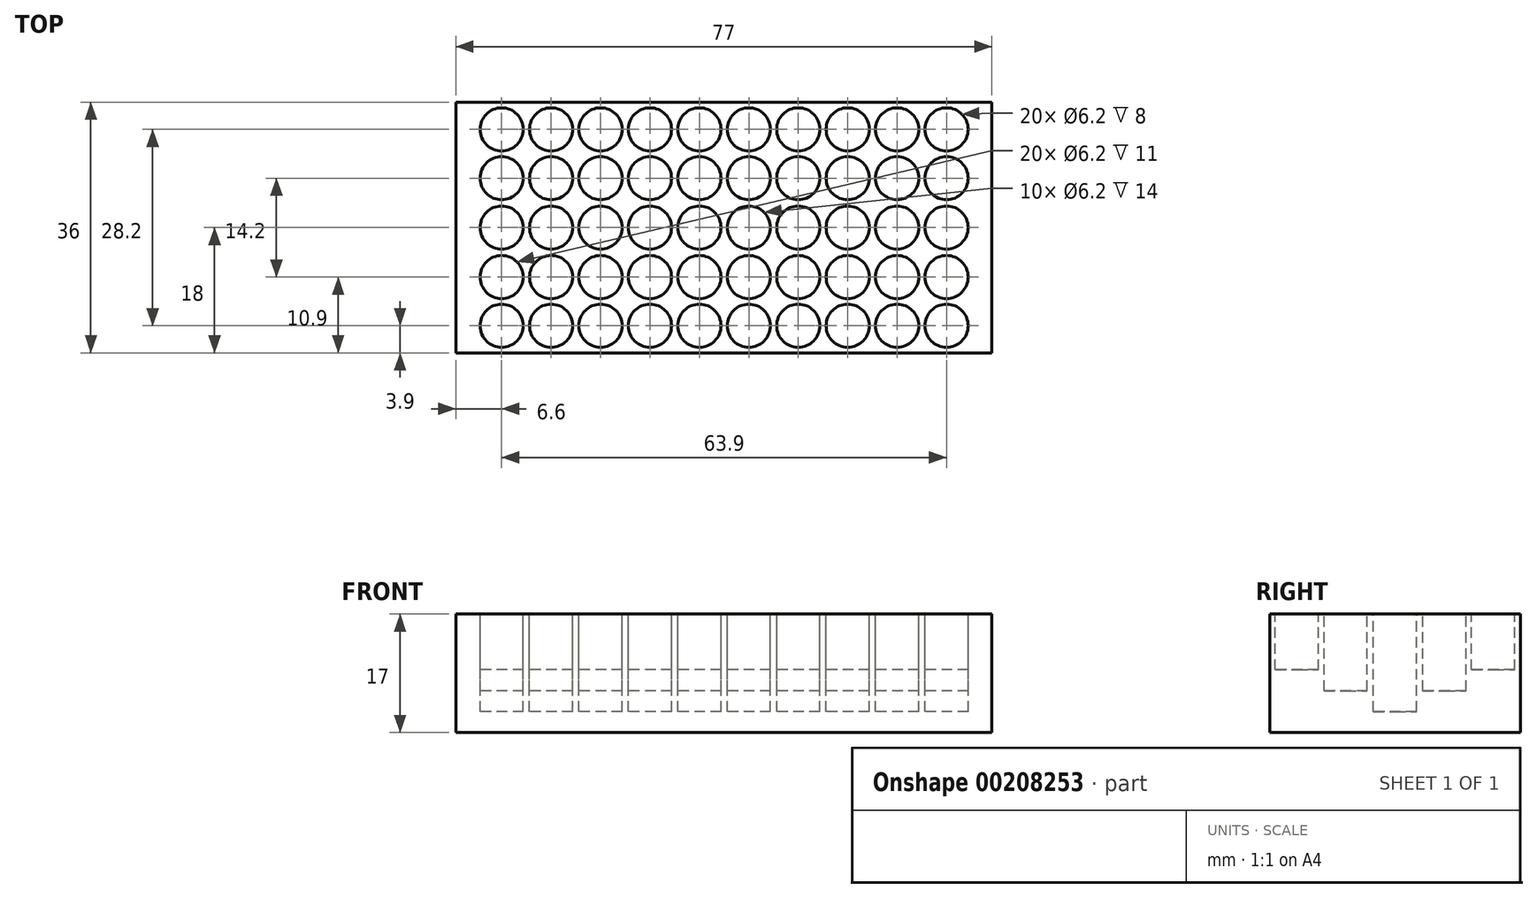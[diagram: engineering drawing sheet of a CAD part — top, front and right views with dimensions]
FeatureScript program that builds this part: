
annotation { "Feature Type Name" : "Feature", "Feature Type Description" : "" }
export const myFeature = defineFeature(function(context is Context, id is Id, definition is map)
    precondition{}
    {
        {
            var Q0;
            Q0=qCreatedBy(makeId("Top.planeOp"),FACE);
            var sketch = newSketch(context, id + "F0", { "sketchPlane" : qUnion([Q0])});
            skLineSegment(sketch, "E0.bottom", {"start": v(-38.5, 18) * mm, "end": v(38.5, 18) * mm});
            skLineSegment(sketch, "E0.top", {"start": v(-38.5, -18) * mm, "end": v(38.5, -18) * mm});
            skLineSegment(sketch, "E0.left", {"start": v(-38.5, 18) * mm, "end": v(-38.5, -18) * mm});
            skLineSegment(sketch, "E0.right", {"start": v(38.5, 18) * mm, "end": v(38.5, -18) * mm});
            skSolve(sketch);
        }
        {
            var Q0;
            Q0 = qSketchRegion(id + "F0", true);
            extrude(context, id + "F1", {"entities" : qUnion([Q0]), "depth" : 17 * mm});
        }
        {
            var Q0;
            Q0=makeQuery(id+"F1.opExtrude","CAP_FACE",FACE,{"disambiguationData":[OSD([sQuery(id+"F0.wireOp",EDGE,"E0.bottom"),sQuery(id+"F0.wireOp",EDGE,"E0.top"),sQuery(id+"F0.wireOp",EDGE,"E0.left"),sQuery(id+"F0.wireOp",EDGE,"E0.right")])],"isStart":false});
            var sketch = newSketch(context, id + "F2", { "sketchPlane" : qUnion([Q0])});
            skCircle(sketch, "E1", {"center": v(-31.9, 14.1) * mm, "radius": 3.1 * mm});
            skCircle(sketch, "E2.1.0.0", {"center": v(-24.8, 14.1) * mm, "radius": 3.1 * mm});
            skCircle(sketch, "E2.2.0.0", {"center": v(-17.7, 14.1) * mm, "radius": 3.1 * mm});
            skCircle(sketch, "E2.3.0.0", {"center": v(-10.6, 14.1) * mm, "radius": 3.1 * mm});
            skCircle(sketch, "E2.4.0.0", {"center": v(-3.5, 14.1) * mm, "radius": 3.1 * mm});
            skCircle(sketch, "E2.5.0.0", {"center": v(3.6, 14.1) * mm, "radius": 3.1 * mm});
            skCircle(sketch, "E2.6.0.0", {"center": v(10.7, 14.1) * mm, "radius": 3.1 * mm});
            skCircle(sketch, "E2.7.0.0", {"center": v(17.8, 14.1) * mm, "radius": 3.1 * mm});
            skCircle(sketch, "E2.8.0.0", {"center": v(24.9, 14.1) * mm, "radius": 3.1 * mm});
            skCircle(sketch, "E2.9.0.0", {"center": v(32, 14.1) * mm, "radius": 3.1 * mm});
            skLineSegment(sketch, "E2.direction1", {"start": v(-31.9, 14.1) * mm, "end": v(-24.8, 14.1) * mm, "construction": true});
            skCircle(sketch, "E3.MirrorC", {"center": v(-31.9, -14.1) * mm, "radius": 3.1 * mm});
            skCircle(sketch, "E4.MirrorC", {"center": v(-24.8, -14.1) * mm, "radius": 3.1 * mm});
            skCircle(sketch, "E5.MirrorC", {"center": v(-17.7, -14.1) * mm, "radius": 3.1 * mm});
            skCircle(sketch, "E6.MirrorC", {"center": v(-10.6, -14.1) * mm, "radius": 3.1 * mm});
            skCircle(sketch, "E7.MirrorC", {"center": v(-3.5, -14.1) * mm, "radius": 3.1 * mm});
            skCircle(sketch, "E8.MirrorC", {"center": v(3.6, -14.1) * mm, "radius": 3.1 * mm});
            skCircle(sketch, "E9.MirrorC", {"center": v(10.7, -14.1) * mm, "radius": 3.1 * mm});
            skCircle(sketch, "E10.MirrorC", {"center": v(17.8, -14.1) * mm, "radius": 3.1 * mm});
            skCircle(sketch, "E11.MirrorC", {"center": v(24.9, -14.1) * mm, "radius": 3.1 * mm});
            skCircle(sketch, "E12.MirrorC", {"center": v(32, -14.1) * mm, "radius": 3.1 * mm});
            skSolve(sketch);
        }
        {
            var Q0;
            Q0 = qSketchRegion(id + "F2", true);
            extrude(context, id + "F3", {"entities" : qUnion([Q0]), "operationType" : NewBodyOperationType.REMOVE, "oppositeDirection" : true, "depth" : 8 * mm});
        }
        {
            var Q0;
            Q0=makeQuery(id+"F1.opExtrude","CAP_FACE",FACE,{"disambiguationData":[OSD([sQuery(id+"F0.wireOp",EDGE,"E0.bottom"),sQuery(id+"F0.wireOp",EDGE,"E0.top"),sQuery(id+"F0.wireOp",EDGE,"E0.left"),sQuery(id+"F0.wireOp",EDGE,"E0.right")])],"isStart":false});
            var sketch = newSketch(context, id + "F4", { "sketchPlane" : qUnion([Q0])});
            skCircle(sketch, "E13", {"center": v(-31.9, 7.1) * mm, "radius": 3.1 * mm});
            skPoint(sketch, "E14", {"position": v(-31.9, 14.1) * mm});
            skCircle(sketch, "E15.1.0.0", {"center": v(-24.8, 7.1) * mm, "radius": 3.1 * mm});
            skCircle(sketch, "E15.2.0.0", {"center": v(-17.7, 7.1) * mm, "radius": 3.1 * mm});
            skCircle(sketch, "E15.3.0.0", {"center": v(-10.6, 7.1) * mm, "radius": 3.1 * mm});
            skCircle(sketch, "E15.4.0.0", {"center": v(-3.5, 7.1) * mm, "radius": 3.1 * mm});
            skCircle(sketch, "E15.5.0.0", {"center": v(3.6, 7.1) * mm, "radius": 3.1 * mm});
            skCircle(sketch, "E15.6.0.0", {"center": v(10.7, 7.1) * mm, "radius": 3.1 * mm});
            skCircle(sketch, "E15.7.0.0", {"center": v(17.8, 7.1) * mm, "radius": 3.1 * mm});
            skCircle(sketch, "E15.8.0.0", {"center": v(24.9, 7.1) * mm, "radius": 3.1 * mm});
            skCircle(sketch, "E15.9.0.0", {"center": v(32, 7.1) * mm, "radius": 3.1 * mm});
            skLineSegment(sketch, "E15.direction1", {"start": v(-31.9, 7.1) * mm, "end": v(-24.8, 7.1) * mm, "construction": true});
            skCircle(sketch, "E16.MirrorC", {"center": v(-31.9, -7.1) * mm, "radius": 3.1 * mm});
            skCircle(sketch, "E17.MirrorC", {"center": v(-24.8, -7.1) * mm, "radius": 3.1 * mm});
            skCircle(sketch, "E18.MirrorC", {"center": v(-17.7, -7.1) * mm, "radius": 3.1 * mm});
            skCircle(sketch, "E19.MirrorC", {"center": v(-10.6, -7.1) * mm, "radius": 3.1 * mm});
            skCircle(sketch, "E20.MirrorC", {"center": v(-3.5, -7.1) * mm, "radius": 3.1 * mm});
            skCircle(sketch, "E21.MirrorC", {"center": v(3.6, -7.1) * mm, "radius": 3.1 * mm});
            skCircle(sketch, "E22.MirrorC", {"center": v(10.7, -7.1) * mm, "radius": 3.1 * mm});
            skCircle(sketch, "E23.MirrorC", {"center": v(17.8, -7.1) * mm, "radius": 3.1 * mm});
            skCircle(sketch, "E24.MirrorC", {"center": v(24.9, -7.1) * mm, "radius": 3.1 * mm});
            skCircle(sketch, "E25.MirrorC", {"center": v(32, -7.1) * mm, "radius": 3.1 * mm});
            skSolve(sketch);
        }
        {
            var Q0;
            Q0 = qSketchRegion(id + "F4", true);
            extrude(context, id + "F5", {"entities" : qUnion([Q0]), "operationType" : NewBodyOperationType.REMOVE, "oppositeDirection" : true, "depth" : 11 * mm});
        }
        {
            var Q0;
            Q0=makeQuery(id+"F1.opExtrude","CAP_FACE",FACE,{"disambiguationData":[OSD([sQuery(id+"F0.wireOp",EDGE,"E0.bottom"),sQuery(id+"F0.wireOp",EDGE,"E0.top"),sQuery(id+"F0.wireOp",EDGE,"E0.left"),sQuery(id+"F0.wireOp",EDGE,"E0.right")])],"isStart":false});
            var sketch = newSketch(context, id + "F6", { "sketchPlane" : qUnion([Q0])});
            skCircle(sketch, "E26", {"center": v(-31.9, 0) * mm, "radius": 3.1 * mm});
            skCircle(sketch, "E27.1.0.0", {"center": v(-24.8, 0) * mm, "radius": 3.1 * mm});
            skCircle(sketch, "E27.2.0.0", {"center": v(-17.7, 0) * mm, "radius": 3.1 * mm});
            skCircle(sketch, "E27.3.0.0", {"center": v(-10.6, 0) * mm, "radius": 3.1 * mm});
            skCircle(sketch, "E27.4.0.0", {"center": v(-3.5, 0) * mm, "radius": 3.1 * mm});
            skCircle(sketch, "E27.5.0.0", {"center": v(3.6, 0) * mm, "radius": 3.1 * mm});
            skCircle(sketch, "E27.6.0.0", {"center": v(10.7, 0) * mm, "radius": 3.1 * mm});
            skCircle(sketch, "E27.7.0.0", {"center": v(17.8, 0) * mm, "radius": 3.1 * mm});
            skCircle(sketch, "E27.8.0.0", {"center": v(24.9, 0) * mm, "radius": 3.1 * mm});
            skCircle(sketch, "E27.9.0.0", {"center": v(32, 0) * mm, "radius": 3.1 * mm});
            skLineSegment(sketch, "E27.direction1", {"start": v(-31.9, 0) * mm, "end": v(-24.8, 0) * mm, "construction": true});
            skSolve(sketch);
        }
        {
            var Q0;
            Q0 = qSketchRegion(id + "F6", true);
            extrude(context, id + "F7", {"entities" : qUnion([Q0]), "operationType" : NewBodyOperationType.REMOVE, "oppositeDirection" : true, "depth" : 14 * mm});
        }
    });
